# Revit family: FantiniCosmi_BIM_C57CT
name_source: partatom
category: Modelli generici
units: mm (PartAtom-declared; Revit-internal decimal feet)

## family parameters
Basato su piano di lavoro = No
Condiviso = No
Punto di calcolo locali = No
Può ospitare armatura = No
Quota connettore circolare = Usa diametro
Sempre verticale = Sì
Taglio con vuoti quando caricato = No
Tipo di parte = Normale

## types (1)
- Standard
    Area = 0,14 m²
    Body admissible ambient temperature = 45 °C
    Catalog web link = https://www.fantinicosmi.it
    Color = White
    Comfort and economy regulation range = 2 ÷ 62 °C
    Descrizione = Weekly programmable thermostats, with batteries
    Differential = 0,25 K
    Extra interface = CT3MA
    Part Number = FantiniCosmi_BIM_C57CT
    Preset antifreeze = 5 °C
    Prospetto di default = 0 mm  [stored 0 ft]
    Type of action = 1BU (micro disconnection)

note: [stored X ft] marks values corroborated as IEEE doubles in the binary element streams (Revit-internal decimal feet)

## geometry (parser evidence)
native form markers: Sweep x3
no freeform markers — native parametric forms only
